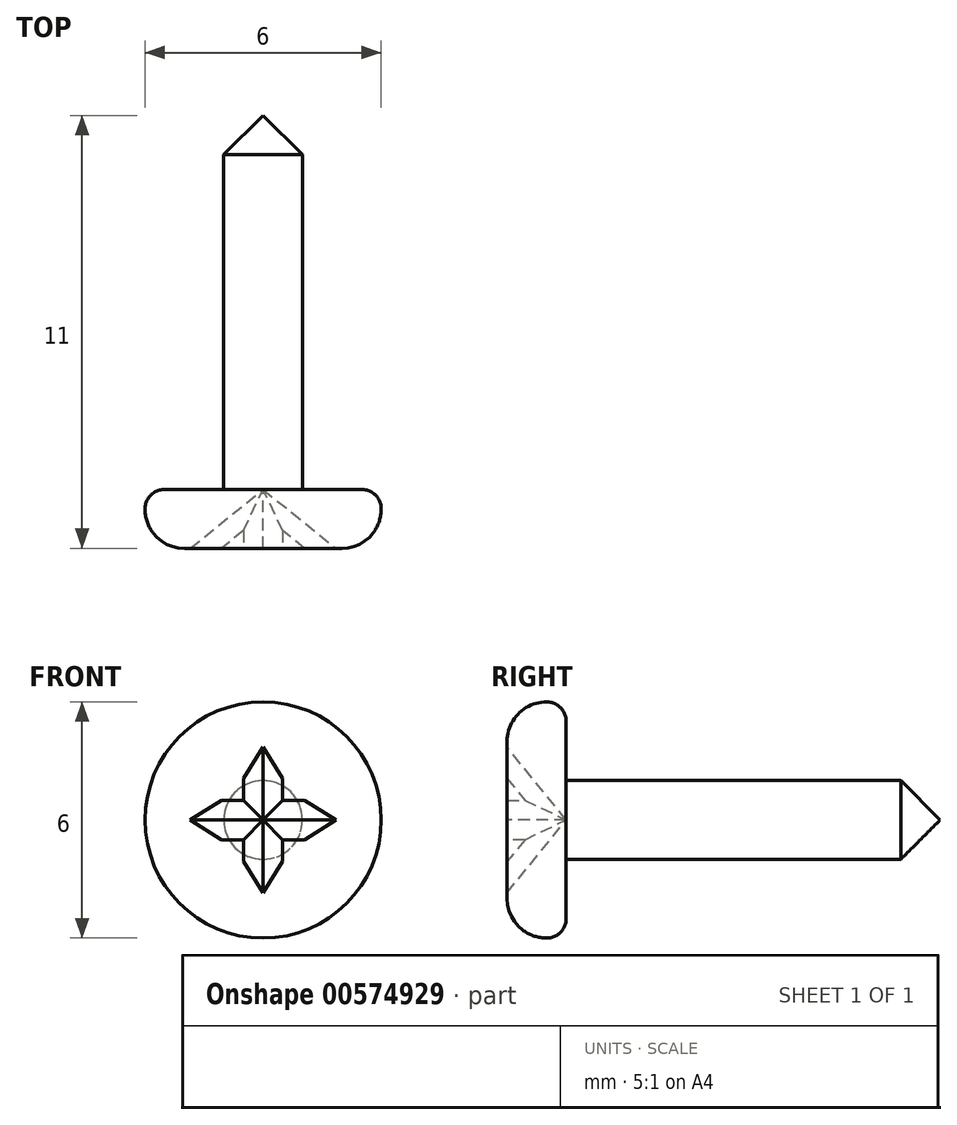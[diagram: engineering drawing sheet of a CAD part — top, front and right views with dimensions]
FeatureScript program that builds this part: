
annotation { "Feature Type Name" : "Feature", "Feature Type Description" : "" }
export const myFeature = defineFeature(function(context is Context, id is Id, definition is map)
    precondition{}
    {
        {
            var Q0;
            Q0=qCreatedBy(makeId("Right.planeOp"),FACE);
            var sketch = newSketch(context, id + "F0", { "sketchPlane" : qUnion([Q0])});
            skLineSegment(sketch, "E0", {"start": v(0, 0) * mm, "end": v(0, 2) * mm});
            skLineSegment(sketch, "E1", {"start": v(1, 3) * mm, "end": v(1, 3) * mm});
            skLineSegment(sketch, "E2", {"start": v(1.5, 2.5) * mm, "end": v(1.5, 1) * mm});
            skLineSegment(sketch, "E3", {"start": v(1.5, 1) * mm, "end": v(11, 1) * mm});
            skLineSegment(sketch, "E4", {"start": v(11, 1) * mm, "end": v(11, 0) * mm});
            skPoint(sketch, "E5.visualSharp", {"position": v(0, 3) * mm});
            skArc(sketch, "E5.filletArc", {"start": v(1, 3) * mm, "mid": v(0.3, 2.7) * mm, "end": v(0, 2) * mm});
            skPoint(sketch, "E6.visualSharp", {"position": v(1.5, 3) * mm});
            skArc(sketch, "E6.filletArc", {"start": v(1.5, 2.5) * mm, "mid": v(1.35, 2.85) * mm, "end": v(1, 3) * mm});
            skLineSegment(sketch, "E7", {"start": v(0, 0) * mm, "end": v(11, 0) * mm});
            skLineSegment(sketch, "E8", {"start": v(0, 0) * mm, "end": v(-8.62, 0) * mm, "construction": true});
            skSolve(sketch);
        }
        {
            var Q0;
            Q0=makeQuery(id+"F0.imprint","IMPRINT",FACE,{"disambiguationData":[TD([[makeQuery(id+"F0.imprint","IMPRINT",EDGE,{"derivedFrom":sQuery(id+"F0.wireOp",EDGE,"E0")}),-1.0]])]});
            var Q1;
            Q1=sQuery(id+"F0.wireOp",EDGE,"E8");
            revolve(context, id + "F1", {"entities" : qUnion([Q0]), "axis" : qUnion([Q1]), "revolveType" : RevolveType.FULL});
        }
        {
            var Q0;
            Q0=makeQuery(id+"F1.opRevolve","SWEPT_EDGE",EDGE,{"disambiguationData":[OSD([sQuery(id+"F0.wireOp",EDGE,"E3"),sQuery(id+"F0.wireOp",EDGE,"E4")])]});
            chamfer(context, id + "F2", {"entities" : qUnion([Q0]), "width" : 1 * mm, "tangentPropagation" : true});
        }
        {
            var Q0;
            Q0=qCreatedBy(makeId("Right.planeOp"),FACE);
            var sketch = newSketch(context, id + "F3", { "sketchPlane" : qUnion([Q0])});
            skLineSegment(sketch, "E9", {"start": v(0, 1.85) * mm, "end": v(0, -1.85) * mm});
            skLineSegment(sketch, "E10", {"start": v(0, -1.85) * mm, "end": v(1.5, 0) * mm});
            skLineSegment(sketch, "E11", {"start": v(1.5, 0) * mm, "end": v(0, 1.85) * mm});
            skSolve(sketch);
        }
        {
            var Q0;
            Q0 = qSketchRegion(id + "F3", true);
            extrude(context, id + "F4", {"entities" : qUnion([Q0]), "operationType" : NewBodyOperationType.REMOVE, "depth" : 1 * mm, "offsetDistance" : 25 * mm, "symmetric" : true});
        }
        {
            var Q0;
            Q0=makeQuery(id+"F4.boolean.opBoolean","COPY",EDGE,{"derivedFrom":makeQuery(id+"F4.opExtrude","CAP_EDGE",EDGE,{"disambiguationData":[OSD([sQuery(id+"F3.wireOp",EDGE,"E10")])],"isStart":false})});
            var Q1;
            Q1=makeQuery(id+"F4.boolean.opBoolean","COPY",EDGE,{"derivedFrom":makeQuery(id+"F4.opExtrude","CAP_EDGE",EDGE,{"disambiguationData":[OSD([sQuery(id+"F3.wireOp",EDGE,"E10")])],"isStart":true})});
            var Q2;
            Q2=makeQuery(id+"F4.boolean.opBoolean","COPY",EDGE,{"derivedFrom":makeQuery(id+"F4.opExtrude","CAP_EDGE",EDGE,{"disambiguationData":[OSD([sQuery(id+"F3.wireOp",EDGE,"E11")])],"isStart":true})});
            var Q3;
            Q3=makeQuery(id+"F4.boolean.opBoolean","COPY",EDGE,{"derivedFrom":makeQuery(id+"F4.opExtrude","CAP_EDGE",EDGE,{"disambiguationData":[OSD([sQuery(id+"F3.wireOp",EDGE,"E11")])],"isStart":false})});
            chamfer(context, id + "F5", {"entities" : qUnion([Q0, Q1, Q2, Q3]), "width" : 0.5 * mm});
        }
        {
            var Q0;
            Q0=qCreatedBy(makeId("Top.planeOp"),FACE);
            var sketch = newSketch(context, id + "F6", { "sketchPlane" : qUnion([Q0])});
            skLineSegment(sketch, "E12", {"start": v(-1.85, 0) * mm, "end": v(1.85, 0) * mm});
            skLineSegment(sketch, "E13", {"start": v(1.85, 0) * mm, "end": v(0, 1.5) * mm});
            skLineSegment(sketch, "E14", {"start": v(0, 1.5) * mm, "end": v(-1.85, 0) * mm});
            skSolve(sketch);
        }
        {
            var Q0;
            Q0 = qSketchRegion(id + "F6", true);
            extrude(context, id + "F7", {"entities" : qUnion([Q0]), "operationType" : NewBodyOperationType.REMOVE, "oppositeDirection" : true, "depth" : 1 * mm, "offsetDistance" : 25 * mm, "symmetric" : true});
        }
        {
            var Q0;
            Q0=makeQuery(id+"F7.boolean.opBoolean","COPY",EDGE,{"derivedFrom":makeQuery(id+"F7.opExtrude","CAP_EDGE",EDGE,{"disambiguationData":[OSD([sQuery(id+"F6.wireOp",EDGE,"E13")])],"isStart":false})});
            var Q1;
            Q1=makeQuery(id+"F7.boolean.opBoolean","COPY",EDGE,{"derivedFrom":makeQuery(id+"F7.opExtrude","CAP_EDGE",EDGE,{"disambiguationData":[OSD([sQuery(id+"F6.wireOp",EDGE,"E14")])],"isStart":false})});
            var Q2;
            Q2=makeQuery(id+"F7.boolean.opBoolean","COPY",EDGE,{"derivedFrom":makeQuery(id+"F7.opExtrude","CAP_EDGE",EDGE,{"disambiguationData":[OSD([sQuery(id+"F6.wireOp",EDGE,"E13")])],"isStart":true})});
            var Q3;
            Q3=makeQuery(id+"F7.boolean.opBoolean","COPY",EDGE,{"derivedFrom":makeQuery(id+"F7.opExtrude","CAP_EDGE",EDGE,{"disambiguationData":[OSD([sQuery(id+"F6.wireOp",EDGE,"E14")])],"isStart":true})});
            chamfer(context, id + "F8", {"entities" : qUnion([Q0, Q1, Q2, Q3]), "width" : 0.5 * mm});
        }
    });
